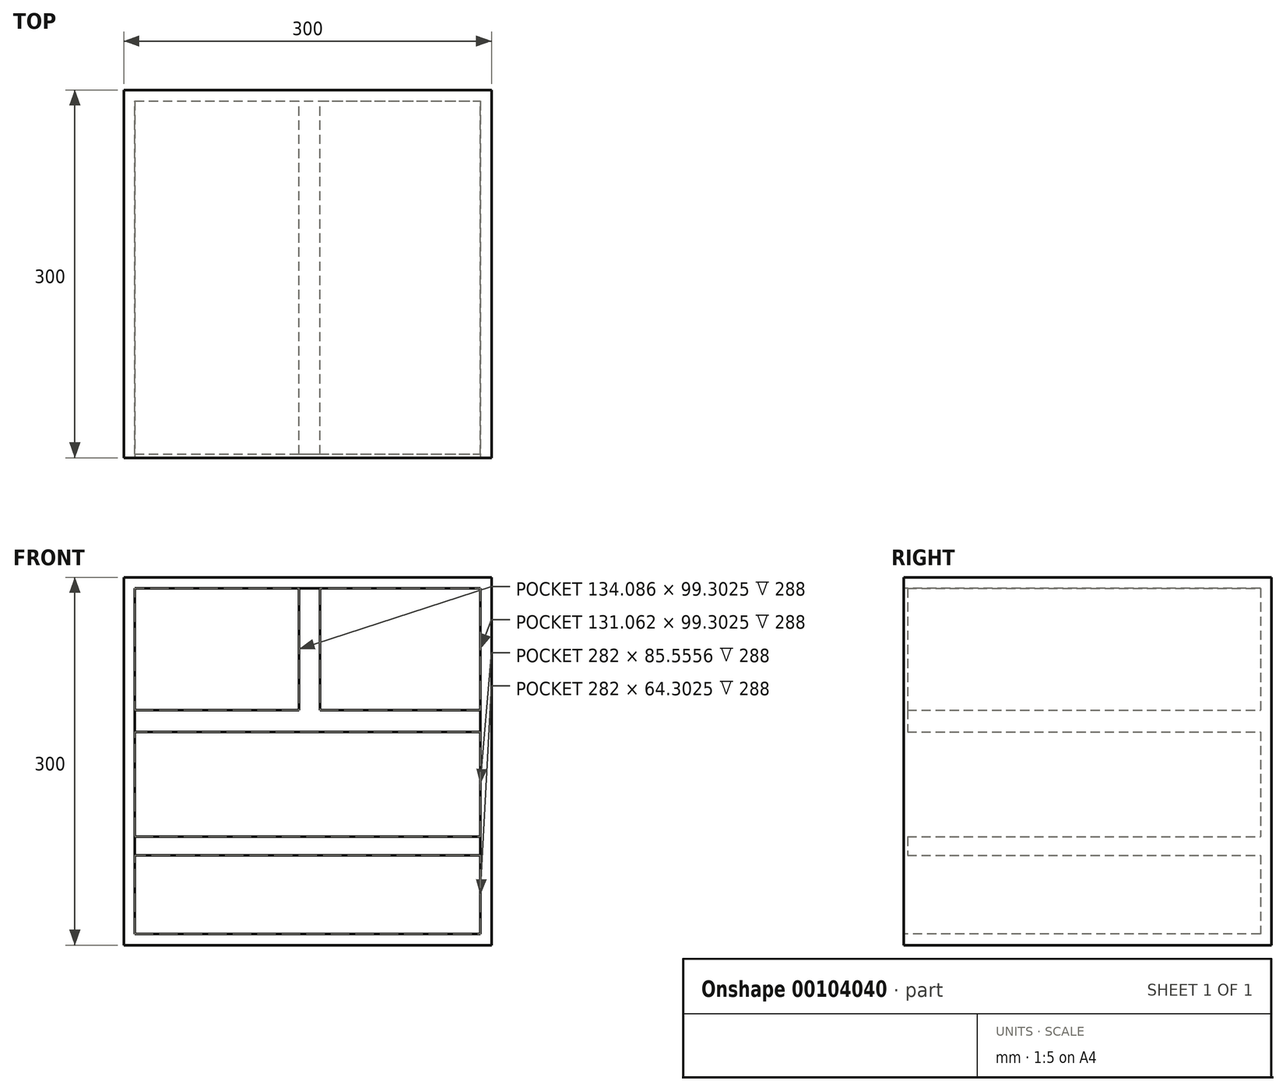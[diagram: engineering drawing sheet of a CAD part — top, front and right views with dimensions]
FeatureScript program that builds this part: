
annotation { "Feature Type Name" : "Feature", "Feature Type Description" : "" }
export const myFeature = defineFeature(function(context is Context, id is Id, definition is map)
    precondition{}
    {
        {
            var Q0;
            Q0=qCreatedBy(makeId("Front.planeOp"),FACE);
            var sketch = newSketch(context, id + "F0", { "sketchPlane" : qUnion([Q0])});
            skLineSegment(sketch, "E0.bottom", {"start": v(-150, 150) * mm, "end": v(150, 150) * mm});
            skLineSegment(sketch, "E0.top", {"start": v(-150, -150) * mm, "end": v(150, -150) * mm});
            skLineSegment(sketch, "E0.left", {"start": v(-150, 150) * mm, "end": v(-150, -150) * mm});
            skLineSegment(sketch, "E0.right", {"start": v(150, 150) * mm, "end": v(150, -150) * mm});
            skPoint(sketch, "E0.middle", {"position": v(0, 0) * mm});
            skSolve(sketch);
        }
        {
            var Q0;
            Q0=makeQuery(id+"F0.imprint","IMPRINT",FACE,{"disambiguationData":[TD([[makeQuery(id+"F0.imprint","IMPRINT",EDGE,{"derivedFrom":sQuery(id+"F0.wireOp",EDGE,"E0.bottom")}),-1.0]])]});
            extrude(context, id + "F1", {"entities" : qUnion([Q0]), "oppositeDirection" : true, "depth" : 300 * mm});
        }
        {
            var Q0;
            Q0=makeQuery(id+"F1.opExtrude","CAP_FACE",FACE,{"disambiguationData":[OSD([sQuery(id+"F0.wireOp",EDGE,"E0.bottom"),sQuery(id+"F0.wireOp",EDGE,"E0.top"),sQuery(id+"F0.wireOp",EDGE,"E0.left"),sQuery(id+"F0.wireOp",EDGE,"E0.right")])],"isStart":true});
            shell(context, id + "F2", {"entities" : qUnion([Q0]), "thickness" : 9 * mm});
        }
        {
            var Q0;
            Q0=makeQuery(id+"F2.opShell","OFFSET_FACE",FACE,{"disambiguationData":[OSD([sQuery(id+"F0.wireOp",EDGE,"E0.bottom"),sQuery(id+"F0.wireOp",EDGE,"E0.top"),sQuery(id+"F0.wireOp",EDGE,"E0.left"),sQuery(id+"F0.wireOp",EDGE,"E0.right")])]});
            var sketch = newSketch(context, id + "F3", { "sketchPlane" : qUnion([Q0])});
            skLineSegment(sketch, "E1.bottom", {"start": v(-146.48, -61.57) * mm, "end": v(146.48, -61.57) * mm});
            skLineSegment(sketch, "E1.top", {"start": v(-146.48, -76.7) * mm, "end": v(146.48, -76.7) * mm});
            skLineSegment(sketch, "E1.left", {"start": v(-146.48, -61.57) * mm, "end": v(-146.48, -76.7) * mm});
            skLineSegment(sketch, "E1.right", {"start": v(146.48, -61.57) * mm, "end": v(146.48, -76.7) * mm});
            skLineSegment(sketch, "E2.bottom", {"start": v(-148.2, 41.7) * mm, "end": v(145.19, 41.7) * mm});
            skLineSegment(sketch, "E2.top", {"start": v(-148.2, 23.98) * mm, "end": v(145.19, 23.98) * mm});
            skLineSegment(sketch, "E2.left", {"start": v(-148.2, 41.7) * mm, "end": v(-148.2, 23.98) * mm});
            skLineSegment(sketch, "E2.right", {"start": v(145.19, 41.7) * mm, "end": v(145.19, 23.98) * mm});
            skLineSegment(sketch, "E3.bottom", {"start": v(-6.91, 148.43) * mm, "end": v(9.94, 148.43) * mm});
            skLineSegment(sketch, "E3.top", {"start": v(-6.91, 31.33) * mm, "end": v(9.94, 31.33) * mm});
            skLineSegment(sketch, "E3.left", {"start": v(-6.91, 148.43) * mm, "end": v(-6.91, 31.33) * mm});
            skLineSegment(sketch, "E3.right", {"start": v(9.94, 148.43) * mm, "end": v(9.94, 31.33) * mm});
            skSolve(sketch);
        }
        {
            var Q0;
            {var subQ0=sQuery(id+"F3.wireOp",EDGE,"E3.top");Q0=makeQuery(id+"F3.imprint","IMPRINT",FACE,{"disambiguationData":[TD([[makeQuery(id+"F3.imprint","IMPRINT",EDGE,{"derivedFrom":subQ0}),-1.0]])]});}
            var Q1;
            {var subQ0=sQuery(id+"F3.wireOp",EDGE,"E1.bottom");var subQ1=sQuery(id+"F0.wireOp",EDGE,"E0.left");var subQ2=makeQuery(id+"F2.opShell","OFFSET_EDGE",EDGE,{"disambiguationData":[OSD([subQ1]),TDD([makeQuery(id+"F1.opExtrude","CAP_EDGE",EDGE,{"disambiguationData":[OSD([subQ1])],"isStart":false})])]});var subQ3=makeQuery(id+"F3.imprint","INTERSECT",VERTEX,{"derivedFrom":[subQ2,subQ0]});Q1=makeQuery(id+"F3.imprint","IMPRINT",FACE,{"disambiguationData":[TD([[makeQuery(id+"F3.imprint","IMPRINT",EDGE,{"disambiguationData":[TD([[subQ3,-1.0]])],"derivedFrom":subQ0}),-1.0]])]});}
            var Q2;
            {var subQ5=sQuery(id+"F3.wireOp",EDGE,"E3.top");Q2=makeQuery(id+"F3.imprint","IMPRINT",FACE,{"disambiguationData":[TD([[makeQuery(id+"F3.imprint","IMPRINT",EDGE,{"derivedFrom":subQ5}),1.0]])]});}
            var Q3;
            {var subQ0=sQuery(id+"F3.wireOp",EDGE,"E3.left");var subQ1=sQuery(id+"F3.wireOp",EDGE,"E2.bottom");var subQ2=makeQuery(id+"F3.imprint","INTERSECT",VERTEX,{"derivedFrom":[subQ1,subQ0]});Q3=makeQuery(id+"F3.imprint","IMPRINT",FACE,{"disambiguationData":[TD([[makeQuery(id+"F3.imprint","IMPRINT",EDGE,{"disambiguationData":[TD([[subQ2,-1.0]])],"derivedFrom":subQ1}),1.0]])]});}
            extrude(context, id + "F4", {"entities" : qUnion([Q0, Q1, Q2, Q3]), "operationType" : NewBodyOperationType.ADD, "depth" : 288 * mm});
        }
    });
